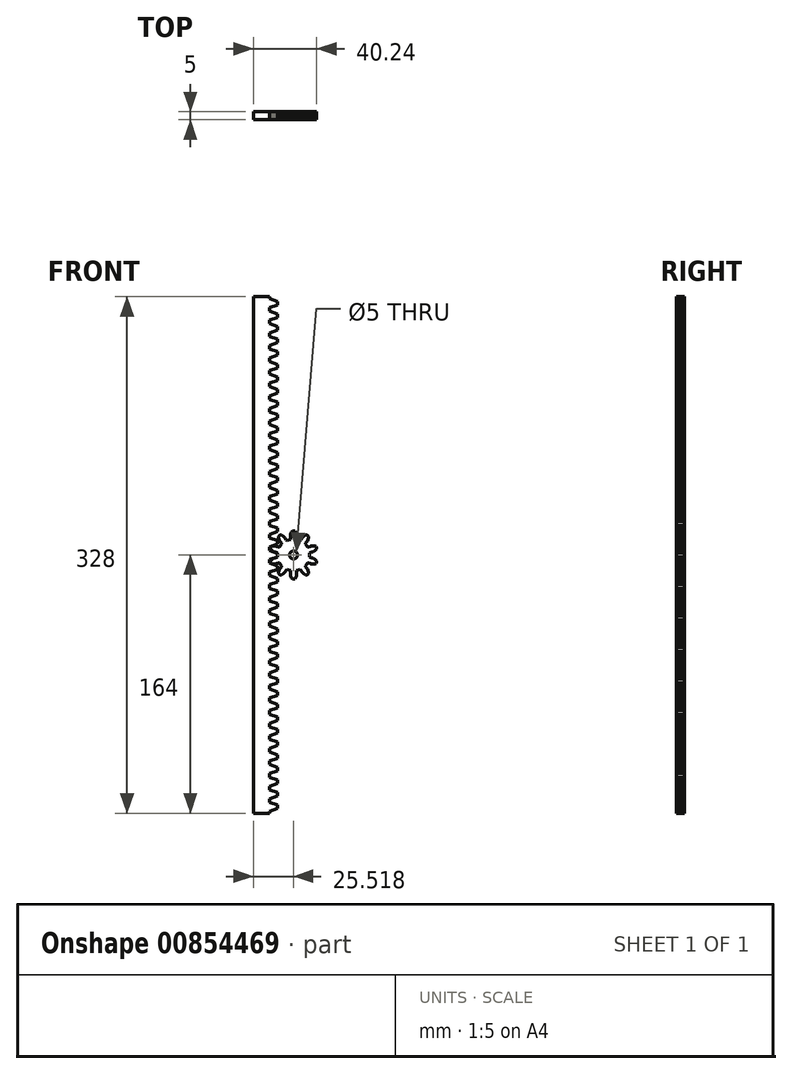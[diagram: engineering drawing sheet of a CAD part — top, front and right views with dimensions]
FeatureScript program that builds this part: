
annotation { "Feature Type Name" : "Feature", "Feature Type Description" : "" }
export const myFeature = defineFeature(function(context is Context, id is Id, definition is map)
    precondition{}
    {
        {
            var Q0;
            Q0=qCreatedBy(makeId("Front.planeOp"),FACE);
            var sketch = newSketch(context, id + "F0", { "sketchPlane" : qUnion([Q0])});
            skLineSegment(sketch, "E0", {"start": v(-9.93, -162.87) * mm, "end": v(-4.79, -161.12) * mm});
            skLineSegment(sketch, "E1", {"start": v(-4.79, -161.12) * mm, "end": v(-4.79, -158.88) * mm});
            skLineSegment(sketch, "E2", {"start": v(-4.79, -158.88) * mm, "end": v(-9.93, -157.13) * mm});
            skLineSegment(sketch, "E3", {"start": v(-9.93, -157.13) * mm, "end": v(-9.93, -154.87) * mm});
            skLineSegment(sketch, "E4", {"start": v(-9.93, -154.87) * mm, "end": v(-4.79, -153.12) * mm});
            skLineSegment(sketch, "E5", {"start": v(-4.79, -153.12) * mm, "end": v(-4.79, -150.88) * mm});
            skLineSegment(sketch, "E6", {"start": v(-4.79, -150.88) * mm, "end": v(-9.93, -149.13) * mm});
            skLineSegment(sketch, "E7", {"start": v(-9.93, -149.13) * mm, "end": v(-9.93, -146.87) * mm});
            skLineSegment(sketch, "E8", {"start": v(-9.93, -146.87) * mm, "end": v(-4.79, -145.12) * mm});
            skLineSegment(sketch, "E9", {"start": v(-4.79, -145.12) * mm, "end": v(-4.79, -142.88) * mm});
            skLineSegment(sketch, "E10", {"start": v(-4.79, -142.88) * mm, "end": v(-9.93, -141.13) * mm});
            skLineSegment(sketch, "E11", {"start": v(-9.93, -141.13) * mm, "end": v(-9.93, -138.87) * mm});
            skLineSegment(sketch, "E12", {"start": v(-9.93, -138.87) * mm, "end": v(-4.79, -137.12) * mm});
            skLineSegment(sketch, "E13", {"start": v(-4.79, -137.12) * mm, "end": v(-4.79, -134.88) * mm});
            skLineSegment(sketch, "E14", {"start": v(-4.79, -134.88) * mm, "end": v(-9.93, -133.13) * mm});
            skLineSegment(sketch, "E15", {"start": v(-9.93, -133.13) * mm, "end": v(-9.93, -130.87) * mm});
            skLineSegment(sketch, "E16", {"start": v(-9.93, -130.87) * mm, "end": v(-4.79, -129.12) * mm});
            skLineSegment(sketch, "E17", {"start": v(-4.79, -129.12) * mm, "end": v(-4.79, -126.88) * mm});
            skLineSegment(sketch, "E18", {"start": v(-4.79, -126.88) * mm, "end": v(-9.93, -125.13) * mm});
            skLineSegment(sketch, "E19", {"start": v(-9.93, -125.13) * mm, "end": v(-9.93, -122.87) * mm});
            skLineSegment(sketch, "E20", {"start": v(-9.93, -122.87) * mm, "end": v(-4.79, -121.12) * mm});
            skLineSegment(sketch, "E21", {"start": v(-4.79, -121.12) * mm, "end": v(-4.79, -118.88) * mm});
            skLineSegment(sketch, "E22", {"start": v(-4.79, -118.88) * mm, "end": v(-9.93, -117.13) * mm});
            skLineSegment(sketch, "E23", {"start": v(-9.93, -117.13) * mm, "end": v(-9.93, -114.87) * mm});
            skLineSegment(sketch, "E24", {"start": v(-9.93, -114.87) * mm, "end": v(-4.79, -113.12) * mm});
            skLineSegment(sketch, "E25", {"start": v(-4.79, -113.12) * mm, "end": v(-4.79, -110.88) * mm});
            skLineSegment(sketch, "E26", {"start": v(-4.79, -110.88) * mm, "end": v(-9.93, -109.13) * mm});
            skLineSegment(sketch, "E27", {"start": v(-9.93, -109.13) * mm, "end": v(-9.93, -106.87) * mm});
            skLineSegment(sketch, "E28", {"start": v(-9.93, -106.87) * mm, "end": v(-4.79, -105.12) * mm});
            skLineSegment(sketch, "E29", {"start": v(-4.79, -105.12) * mm, "end": v(-4.79, -102.88) * mm});
            skLineSegment(sketch, "E30", {"start": v(-4.79, -102.88) * mm, "end": v(-9.93, -101.13) * mm});
            skLineSegment(sketch, "E31", {"start": v(-9.93, -101.13) * mm, "end": v(-9.93, -98.87) * mm});
            skLineSegment(sketch, "E32", {"start": v(-9.93, -98.87) * mm, "end": v(-4.79, -97.12) * mm});
            skLineSegment(sketch, "E33", {"start": v(-4.79, -97.12) * mm, "end": v(-4.79, -94.88) * mm});
            skLineSegment(sketch, "E34", {"start": v(-4.79, -94.88) * mm, "end": v(-9.93, -93.13) * mm});
            skLineSegment(sketch, "E35", {"start": v(-9.93, -93.13) * mm, "end": v(-9.93, -90.87) * mm});
            skLineSegment(sketch, "E36", {"start": v(-9.93, -90.87) * mm, "end": v(-4.79, -89.12) * mm});
            skLineSegment(sketch, "E37", {"start": v(-4.79, -89.12) * mm, "end": v(-4.79, -86.88) * mm});
            skLineSegment(sketch, "E38", {"start": v(-4.79, -86.88) * mm, "end": v(-9.93, -85.13) * mm});
            skLineSegment(sketch, "E39", {"start": v(-9.93, -85.13) * mm, "end": v(-9.93, -82.87) * mm});
            skLineSegment(sketch, "E40", {"start": v(-9.93, -82.87) * mm, "end": v(-4.79, -81.12) * mm});
            skLineSegment(sketch, "E41", {"start": v(-4.79, -81.12) * mm, "end": v(-4.79, -78.88) * mm});
            skLineSegment(sketch, "E42", {"start": v(-4.79, -78.88) * mm, "end": v(-9.93, -77.13) * mm});
            skLineSegment(sketch, "E43", {"start": v(-9.93, -77.13) * mm, "end": v(-9.93, -74.87) * mm});
            skLineSegment(sketch, "E44", {"start": v(-9.93, -74.87) * mm, "end": v(-4.79, -73.12) * mm});
            skLineSegment(sketch, "E45", {"start": v(-4.79, -73.12) * mm, "end": v(-4.79, -70.88) * mm});
            skLineSegment(sketch, "E46", {"start": v(-4.79, -70.88) * mm, "end": v(-9.93, -69.13) * mm});
            skLineSegment(sketch, "E47", {"start": v(-9.93, -69.13) * mm, "end": v(-9.93, -66.87) * mm});
            skLineSegment(sketch, "E48", {"start": v(-9.93, -66.87) * mm, "end": v(-4.79, -65.12) * mm});
            skLineSegment(sketch, "E49", {"start": v(-4.79, -65.12) * mm, "end": v(-4.79, -62.88) * mm});
            skLineSegment(sketch, "E50", {"start": v(-4.79, -62.88) * mm, "end": v(-9.93, -61.13) * mm});
            skLineSegment(sketch, "E51", {"start": v(-9.93, -61.13) * mm, "end": v(-9.93, -58.87) * mm});
            skLineSegment(sketch, "E52", {"start": v(-9.93, -58.87) * mm, "end": v(-4.79, -57.12) * mm});
            skLineSegment(sketch, "E53", {"start": v(-4.79, -57.12) * mm, "end": v(-4.79, -54.88) * mm});
            skLineSegment(sketch, "E54", {"start": v(-4.79, -54.88) * mm, "end": v(-9.93, -53.13) * mm});
            skLineSegment(sketch, "E55", {"start": v(-9.93, -53.13) * mm, "end": v(-9.93, -50.87) * mm});
            skLineSegment(sketch, "E56", {"start": v(-9.93, -50.87) * mm, "end": v(-4.79, -49.12) * mm});
            skLineSegment(sketch, "E57", {"start": v(-4.79, -49.12) * mm, "end": v(-4.79, -46.88) * mm});
            skLineSegment(sketch, "E58", {"start": v(-4.79, -46.88) * mm, "end": v(-9.93, -45.13) * mm});
            skLineSegment(sketch, "E59", {"start": v(-9.93, -45.13) * mm, "end": v(-9.93, -42.87) * mm});
            skLineSegment(sketch, "E60", {"start": v(-9.93, -42.87) * mm, "end": v(-4.79, -41.12) * mm});
            skLineSegment(sketch, "E61", {"start": v(-4.79, -41.12) * mm, "end": v(-4.79, -38.88) * mm});
            skLineSegment(sketch, "E62", {"start": v(-4.79, -38.88) * mm, "end": v(-9.93, -37.13) * mm});
            skLineSegment(sketch, "E63", {"start": v(-9.93, -37.13) * mm, "end": v(-9.93, -34.87) * mm});
            skLineSegment(sketch, "E64", {"start": v(-9.93, -34.87) * mm, "end": v(-4.79, -33.12) * mm});
            skLineSegment(sketch, "E65", {"start": v(-4.79, -33.12) * mm, "end": v(-4.79, -30.88) * mm});
            skLineSegment(sketch, "E66", {"start": v(-4.79, -30.88) * mm, "end": v(-9.93, -29.13) * mm});
            skLineSegment(sketch, "E67", {"start": v(-9.93, -29.13) * mm, "end": v(-9.93, -26.87) * mm});
            skLineSegment(sketch, "E68", {"start": v(-9.93, -26.87) * mm, "end": v(-4.79, -25.12) * mm});
            skLineSegment(sketch, "E69", {"start": v(-4.79, -25.12) * mm, "end": v(-4.79, -22.88) * mm});
            skLineSegment(sketch, "E70", {"start": v(-4.79, -22.88) * mm, "end": v(-9.93, -21.13) * mm});
            skLineSegment(sketch, "E71", {"start": v(-9.93, -21.13) * mm, "end": v(-9.93, -18.87) * mm});
            skLineSegment(sketch, "E72", {"start": v(-9.93, -18.87) * mm, "end": v(-4.79, -17.12) * mm});
            skLineSegment(sketch, "E73", {"start": v(-4.79, -17.12) * mm, "end": v(-4.79, -14.88) * mm});
            skLineSegment(sketch, "E74", {"start": v(-4.79, -14.88) * mm, "end": v(-9.93, -13.13) * mm});
            skLineSegment(sketch, "E75", {"start": v(-9.93, -13.13) * mm, "end": v(-9.93, -10.87) * mm});
            skLineSegment(sketch, "E76", {"start": v(-9.93, -10.87) * mm, "end": v(-4.79, -9.12) * mm});
            skLineSegment(sketch, "E77", {"start": v(-4.79, -9.12) * mm, "end": v(-4.79, -6.88) * mm});
            skLineSegment(sketch, "E78", {"start": v(-4.79, -6.88) * mm, "end": v(-9.93, -5.13) * mm});
            skLineSegment(sketch, "E79", {"start": v(-9.93, -5.13) * mm, "end": v(-9.93, -2.87) * mm});
            skLineSegment(sketch, "E80", {"start": v(-9.93, -2.87) * mm, "end": v(-4.79, -1.12) * mm});
            skLineSegment(sketch, "E81", {"start": v(-4.79, -1.12) * mm, "end": v(-4.79, 1.12) * mm});
            skLineSegment(sketch, "E82", {"start": v(-4.79, 1.12) * mm, "end": v(-9.93, 2.87) * mm});
            skLineSegment(sketch, "E83", {"start": v(-9.93, 2.87) * mm, "end": v(-9.93, 5.13) * mm});
            skLineSegment(sketch, "E84", {"start": v(-9.93, 5.13) * mm, "end": v(-4.79, 6.88) * mm});
            skLineSegment(sketch, "E85", {"start": v(-4.79, 6.88) * mm, "end": v(-4.79, 9.12) * mm});
            skLineSegment(sketch, "E86", {"start": v(-4.79, 9.12) * mm, "end": v(-9.93, 10.87) * mm});
            skLineSegment(sketch, "E87", {"start": v(-9.93, 10.87) * mm, "end": v(-9.93, 13.13) * mm});
            skLineSegment(sketch, "E88", {"start": v(-9.93, 13.13) * mm, "end": v(-4.79, 14.88) * mm});
            skLineSegment(sketch, "E89", {"start": v(-4.79, 14.88) * mm, "end": v(-4.79, 17.12) * mm});
            skLineSegment(sketch, "E90", {"start": v(-4.79, 17.12) * mm, "end": v(-9.93, 18.87) * mm});
            skLineSegment(sketch, "E91", {"start": v(-9.93, 18.87) * mm, "end": v(-9.93, 21.13) * mm});
            skLineSegment(sketch, "E92", {"start": v(-9.93, 21.13) * mm, "end": v(-4.79, 22.88) * mm});
            skLineSegment(sketch, "E93", {"start": v(-4.79, 22.88) * mm, "end": v(-4.79, 25.12) * mm});
            skLineSegment(sketch, "E94", {"start": v(-4.79, 25.12) * mm, "end": v(-9.93, 26.87) * mm});
            skLineSegment(sketch, "E95", {"start": v(-9.93, 26.87) * mm, "end": v(-9.93, 29.13) * mm});
            skLineSegment(sketch, "E96", {"start": v(-9.93, 29.13) * mm, "end": v(-4.79, 30.88) * mm});
            skLineSegment(sketch, "E97", {"start": v(-4.79, 30.88) * mm, "end": v(-4.79, 33.12) * mm});
            skLineSegment(sketch, "E98", {"start": v(-4.79, 33.12) * mm, "end": v(-9.93, 34.87) * mm});
            skLineSegment(sketch, "E99", {"start": v(-9.93, 34.87) * mm, "end": v(-9.93, 37.13) * mm});
            skLineSegment(sketch, "E100", {"start": v(-9.93, 37.13) * mm, "end": v(-4.79, 38.88) * mm});
            skLineSegment(sketch, "E101", {"start": v(-4.79, 38.88) * mm, "end": v(-4.79, 41.12) * mm});
            skLineSegment(sketch, "E102", {"start": v(-4.79, 41.12) * mm, "end": v(-9.93, 42.87) * mm});
            skLineSegment(sketch, "E103", {"start": v(-9.93, 42.87) * mm, "end": v(-9.93, 45.13) * mm});
            skLineSegment(sketch, "E104", {"start": v(-9.93, 45.13) * mm, "end": v(-4.79, 46.88) * mm});
            skLineSegment(sketch, "E105", {"start": v(-4.79, 46.88) * mm, "end": v(-4.79, 49.12) * mm});
            skLineSegment(sketch, "E106", {"start": v(-4.79, 49.12) * mm, "end": v(-9.93, 50.87) * mm});
            skLineSegment(sketch, "E107", {"start": v(-9.93, 50.87) * mm, "end": v(-9.93, 53.13) * mm});
            skLineSegment(sketch, "E108", {"start": v(-9.93, 53.13) * mm, "end": v(-4.79, 54.88) * mm});
            skLineSegment(sketch, "E109", {"start": v(-4.79, 54.88) * mm, "end": v(-4.79, 57.12) * mm});
            skLineSegment(sketch, "E110", {"start": v(-4.79, 57.12) * mm, "end": v(-9.93, 58.87) * mm});
            skLineSegment(sketch, "E111", {"start": v(-9.93, 58.87) * mm, "end": v(-9.93, 61.13) * mm});
            skLineSegment(sketch, "E112", {"start": v(-9.93, 61.13) * mm, "end": v(-4.79, 62.88) * mm});
            skLineSegment(sketch, "E113", {"start": v(-4.79, 62.88) * mm, "end": v(-4.79, 65.12) * mm});
            skLineSegment(sketch, "E114", {"start": v(-4.79, 65.12) * mm, "end": v(-9.93, 66.87) * mm});
            skLineSegment(sketch, "E115", {"start": v(-9.93, 66.87) * mm, "end": v(-9.93, 69.13) * mm});
            skLineSegment(sketch, "E116", {"start": v(-9.93, 69.13) * mm, "end": v(-4.79, 70.88) * mm});
            skLineSegment(sketch, "E117", {"start": v(-4.79, 70.88) * mm, "end": v(-4.79, 73.12) * mm});
            skLineSegment(sketch, "E118", {"start": v(-4.79, 73.12) * mm, "end": v(-9.93, 74.87) * mm});
            skLineSegment(sketch, "E119", {"start": v(-9.93, 74.87) * mm, "end": v(-9.93, 77.13) * mm});
            skLineSegment(sketch, "E120", {"start": v(-9.93, 77.13) * mm, "end": v(-4.79, 78.88) * mm});
            skLineSegment(sketch, "E121", {"start": v(-4.79, 78.88) * mm, "end": v(-4.79, 81.12) * mm});
            skLineSegment(sketch, "E122", {"start": v(-4.79, 81.12) * mm, "end": v(-9.93, 82.87) * mm});
            skLineSegment(sketch, "E123", {"start": v(-9.93, 82.87) * mm, "end": v(-9.93, 85.13) * mm});
            skLineSegment(sketch, "E124", {"start": v(-9.93, 85.13) * mm, "end": v(-4.79, 86.88) * mm});
            skLineSegment(sketch, "E125", {"start": v(-4.79, 86.88) * mm, "end": v(-4.79, 89.12) * mm});
            skLineSegment(sketch, "E126", {"start": v(-4.79, 89.12) * mm, "end": v(-9.93, 90.87) * mm});
            skLineSegment(sketch, "E127", {"start": v(-9.93, 90.87) * mm, "end": v(-9.93, 93.13) * mm});
            skLineSegment(sketch, "E128", {"start": v(-9.93, 93.13) * mm, "end": v(-4.79, 94.88) * mm});
            skLineSegment(sketch, "E129", {"start": v(-4.79, 94.88) * mm, "end": v(-4.79, 97.12) * mm});
            skLineSegment(sketch, "E130", {"start": v(-4.79, 97.12) * mm, "end": v(-9.93, 98.87) * mm});
            skLineSegment(sketch, "E131", {"start": v(-9.93, 98.87) * mm, "end": v(-9.93, 101.13) * mm});
            skLineSegment(sketch, "E132", {"start": v(-9.93, 101.13) * mm, "end": v(-4.79, 102.88) * mm});
            skLineSegment(sketch, "E133", {"start": v(-4.79, 102.88) * mm, "end": v(-4.79, 105.12) * mm});
            skLineSegment(sketch, "E134", {"start": v(-4.79, 105.12) * mm, "end": v(-9.93, 106.87) * mm});
            skLineSegment(sketch, "E135", {"start": v(-9.93, 106.87) * mm, "end": v(-9.93, 109.13) * mm});
            skLineSegment(sketch, "E136", {"start": v(-9.93, 109.13) * mm, "end": v(-4.79, 110.88) * mm});
            skLineSegment(sketch, "E137", {"start": v(-4.79, 110.88) * mm, "end": v(-4.79, 113.12) * mm});
            skLineSegment(sketch, "E138", {"start": v(-4.79, 113.12) * mm, "end": v(-9.93, 114.87) * mm});
            skLineSegment(sketch, "E139", {"start": v(-9.93, 114.87) * mm, "end": v(-9.93, 117.13) * mm});
            skLineSegment(sketch, "E140", {"start": v(-9.93, 117.13) * mm, "end": v(-4.79, 118.88) * mm});
            skLineSegment(sketch, "E141", {"start": v(-4.79, 118.88) * mm, "end": v(-4.79, 121.12) * mm});
            skLineSegment(sketch, "E142", {"start": v(-4.79, 121.12) * mm, "end": v(-9.93, 122.87) * mm});
            skLineSegment(sketch, "E143", {"start": v(-9.93, 122.87) * mm, "end": v(-9.93, 125.13) * mm});
            skLineSegment(sketch, "E144", {"start": v(-9.93, 125.13) * mm, "end": v(-4.79, 126.88) * mm});
            skLineSegment(sketch, "E145", {"start": v(-4.79, 126.88) * mm, "end": v(-4.79, 129.12) * mm});
            skLineSegment(sketch, "E146", {"start": v(-4.79, 129.12) * mm, "end": v(-9.93, 130.87) * mm});
            skLineSegment(sketch, "E147", {"start": v(-9.93, 130.87) * mm, "end": v(-9.93, 133.13) * mm});
            skLineSegment(sketch, "E148", {"start": v(-9.93, 133.13) * mm, "end": v(-4.79, 134.88) * mm});
            skLineSegment(sketch, "E149", {"start": v(-4.79, 134.88) * mm, "end": v(-4.79, 137.12) * mm});
            skLineSegment(sketch, "E150", {"start": v(-4.79, 137.12) * mm, "end": v(-9.93, 138.87) * mm});
            skLineSegment(sketch, "E151", {"start": v(-9.93, 138.87) * mm, "end": v(-9.93, 141.13) * mm});
            skLineSegment(sketch, "E152", {"start": v(-9.93, 141.13) * mm, "end": v(-4.79, 142.88) * mm});
            skLineSegment(sketch, "E153", {"start": v(-4.79, 142.88) * mm, "end": v(-4.79, 145.12) * mm});
            skLineSegment(sketch, "E154", {"start": v(-4.79, 145.12) * mm, "end": v(-9.93, 146.87) * mm});
            skLineSegment(sketch, "E155", {"start": v(-9.93, 146.87) * mm, "end": v(-9.93, 149.13) * mm});
            skLineSegment(sketch, "E156", {"start": v(-9.93, 149.13) * mm, "end": v(-4.79, 150.88) * mm});
            skLineSegment(sketch, "E157", {"start": v(-4.79, 150.88) * mm, "end": v(-4.79, 153.12) * mm});
            skLineSegment(sketch, "E158", {"start": v(-4.79, 153.12) * mm, "end": v(-9.93, 154.87) * mm});
            skLineSegment(sketch, "E159", {"start": v(-9.93, 154.87) * mm, "end": v(-9.93, 157.13) * mm});
            skLineSegment(sketch, "E160", {"start": v(-9.93, 157.13) * mm, "end": v(-4.79, 158.88) * mm});
            skLineSegment(sketch, "E161", {"start": v(-4.79, 158.88) * mm, "end": v(-4.79, 161.12) * mm});
            skLineSegment(sketch, "E162", {"start": v(-4.79, 161.12) * mm, "end": v(-9.93, 162.87) * mm});
            skLineSegment(sketch, "E163", {"start": v(-9.93, 162.87) * mm, "end": v(-9.93, 164) * mm});
            skLineSegment(sketch, "E164", {"start": v(-9.93, 164) * mm, "end": v(-20.12, 164) * mm});
            skLineSegment(sketch, "E165", {"start": v(-20.12, 164) * mm, "end": v(-20.12, -164) * mm});
            skLineSegment(sketch, "E166", {"start": v(-20.12, -164) * mm, "end": v(-9.93, -164) * mm});
            skLineSegment(sketch, "E167", {"start": v(-9.93, -164) * mm, "end": v(-9.93, -162.87) * mm});
            skLineSegment(sketch, "E168", {"start": v(-8.83, 5.46) * mm, "end": v(-9.13, 4.72) * mm});
            skLineSegment(sketch, "E169", {"start": v(-9.13, 4.72) * mm, "end": v(-9.32, 3.94) * mm});
            skLineSegment(sketch, "E170", {"start": v(-9.32, 3.94) * mm, "end": v(-8.99, 3.46) * mm});
            skLineSegment(sketch, "E171", {"start": v(-8.99, 3.46) * mm, "end": v(-7.87, 2.43) * mm});
            skLineSegment(sketch, "E172", {"start": v(-7.87, 2.43) * mm, "end": v(-7.02, 1.92) * mm});
            skLineSegment(sketch, "E173", {"start": v(-7.02, 1.92) * mm, "end": v(-6.61, 1.78) * mm});
            skLineSegment(sketch, "E174", {"start": v(-6.61, 1.78) * mm, "end": v(-6.5, 1.79) * mm});
            skLineSegment(sketch, "E175", {"start": v(-6.5, 1.79) * mm, "end": v(-5.3, 1.61) * mm});
            skLineSegment(sketch, "E176", {"start": v(-5.3, 1.61) * mm, "end": v(-4.74, 1.14) * mm});
            skLineSegment(sketch, "E177", {"start": v(-4.74, 1.14) * mm, "end": v(-4.74, -1.14) * mm});
            skLineSegment(sketch, "E178", {"start": v(-4.74, -1.14) * mm, "end": v(-5.3, -1.61) * mm});
            skLineSegment(sketch, "E179", {"start": v(-5.3, -1.61) * mm, "end": v(-6.5, -1.79) * mm});
            skLineSegment(sketch, "E180", {"start": v(-6.5, -1.79) * mm, "end": v(-6.61, -1.78) * mm});
            skLineSegment(sketch, "E181", {"start": v(-6.61, -1.78) * mm, "end": v(-7.02, -1.92) * mm});
            skLineSegment(sketch, "E182", {"start": v(-7.02, -1.92) * mm, "end": v(-7.87, -2.43) * mm});
            skLineSegment(sketch, "E183", {"start": v(-7.87, -2.43) * mm, "end": v(-8.99, -3.46) * mm});
            skLineSegment(sketch, "E184", {"start": v(-8.99, -3.46) * mm, "end": v(-9.32, -3.94) * mm});
            skLineSegment(sketch, "E185", {"start": v(-9.32, -3.94) * mm, "end": v(-9.13, -4.72) * mm});
            skLineSegment(sketch, "E186", {"start": v(-9.13, -4.72) * mm, "end": v(-8.83, -5.46) * mm});
            skLineSegment(sketch, "E187", {"start": v(-8.83, -5.46) * mm, "end": v(-8.28, -5.65) * mm});
            skLineSegment(sketch, "E188", {"start": v(-8.28, -5.65) * mm, "end": v(-6.76, -5.83) * mm});
            skLineSegment(sketch, "E189", {"start": v(-6.76, -5.83) * mm, "end": v(-5.77, -5.75) * mm});
            skLineSegment(sketch, "E190", {"start": v(-5.77, -5.75) * mm, "end": v(-5.36, -5.62) * mm});
            skLineSegment(sketch, "E191", {"start": v(-5.36, -5.62) * mm, "end": v(-5.27, -5.54) * mm});
            skLineSegment(sketch, "E192", {"start": v(-5.27, -5.54) * mm, "end": v(-4.21, -4.99) * mm});
            skLineSegment(sketch, "E193", {"start": v(-4.21, -4.99) * mm, "end": v(-3.47, -5.04) * mm});
            skLineSegment(sketch, "E194", {"start": v(-3.47, -5.04) * mm, "end": v(-2.13, -6.88) * mm});
            skLineSegment(sketch, "E195", {"start": v(-2.13, -6.88) * mm, "end": v(-2.31, -7.6) * mm});
            skLineSegment(sketch, "E196", {"start": v(-2.31, -7.6) * mm, "end": v(-3.17, -8.44) * mm});
            skLineSegment(sketch, "E197", {"start": v(-3.17, -8.44) * mm, "end": v(-3.27, -8.5) * mm});
            skLineSegment(sketch, "E198", {"start": v(-3.27, -8.5) * mm, "end": v(-3.52, -8.85) * mm});
            skLineSegment(sketch, "E199", {"start": v(-3.52, -8.85) * mm, "end": v(-3.9, -9.76) * mm});
            skLineSegment(sketch, "E200", {"start": v(-3.9, -9.76) * mm, "end": v(-4.2, -11.26) * mm});
            skLineSegment(sketch, "E201", {"start": v(-4.2, -11.26) * mm, "end": v(-4.2, -11.84) * mm});
            skLineSegment(sketch, "E202", {"start": v(-4.2, -11.84) * mm, "end": v(-3.58, -12.36) * mm});
            skLineSegment(sketch, "E203", {"start": v(-3.58, -12.36) * mm, "end": v(-2.9, -12.78) * mm});
            skLineSegment(sketch, "E204", {"start": v(-2.9, -12.78) * mm, "end": v(-2.34, -12.6) * mm});
            skLineSegment(sketch, "E205", {"start": v(-2.34, -12.6) * mm, "end": v(-1.01, -11.87) * mm});
            skLineSegment(sketch, "E206", {"start": v(-1.01, -11.87) * mm, "end": v(-0.26, -11.21) * mm});
            skLineSegment(sketch, "E207", {"start": v(-0.26, -11.21) * mm, "end": v(0, -10.87) * mm});
            skLineSegment(sketch, "E208", {"start": v(0, -10.87) * mm, "end": v(0.02, -10.76) * mm});
            skLineSegment(sketch, "E209", {"start": v(0.02, -10.76) * mm, "end": v(0.55, -9.68) * mm});
            skLineSegment(sketch, "E210", {"start": v(0.55, -9.68) * mm, "end": v(1.18, -9.29) * mm});
            skLineSegment(sketch, "E211", {"start": v(1.18, -9.29) * mm, "end": v(3.35, -10) * mm});
            skLineSegment(sketch, "E212", {"start": v(3.35, -10) * mm, "end": v(3.63, -10.68) * mm});
            skLineSegment(sketch, "E213", {"start": v(3.63, -10.68) * mm, "end": v(3.43, -11.86) * mm});
            skLineSegment(sketch, "E214", {"start": v(3.43, -11.86) * mm, "end": v(3.38, -11.97) * mm});
            skLineSegment(sketch, "E215", {"start": v(3.38, -11.97) * mm, "end": v(3.39, -12.4) * mm});
            skLineSegment(sketch, "E216", {"start": v(3.39, -12.4) * mm, "end": v(3.6, -13.37) * mm});
            skLineSegment(sketch, "E217", {"start": v(3.6, -13.37) * mm, "end": v(4.25, -14.75) * mm});
            skLineSegment(sketch, "E218", {"start": v(4.25, -14.75) * mm, "end": v(4.6, -15.22) * mm});
            skLineSegment(sketch, "E219", {"start": v(4.6, -15.22) * mm, "end": v(5.4, -15.28) * mm});
            skLineSegment(sketch, "E220", {"start": v(5.4, -15.28) * mm, "end": v(6.2, -15.22) * mm});
            skLineSegment(sketch, "E221", {"start": v(6.2, -15.22) * mm, "end": v(6.55, -14.75) * mm});
            skLineSegment(sketch, "E222", {"start": v(6.55, -14.75) * mm, "end": v(7.19, -13.37) * mm});
            skLineSegment(sketch, "E223", {"start": v(7.19, -13.37) * mm, "end": v(7.41, -12.4) * mm});
            skLineSegment(sketch, "E224", {"start": v(7.41, -12.4) * mm, "end": v(7.42, -11.97) * mm});
            skLineSegment(sketch, "E225", {"start": v(7.42, -11.97) * mm, "end": v(7.37, -11.86) * mm});
            skLineSegment(sketch, "E226", {"start": v(7.37, -11.86) * mm, "end": v(7.17, -10.68) * mm});
            skLineSegment(sketch, "E227", {"start": v(7.17, -10.68) * mm, "end": v(7.45, -10) * mm});
            skLineSegment(sketch, "E228", {"start": v(7.45, -10) * mm, "end": v(9.61, -9.29) * mm});
            skLineSegment(sketch, "E229", {"start": v(9.61, -9.29) * mm, "end": v(10.24, -9.68) * mm});
            skLineSegment(sketch, "E230", {"start": v(10.24, -9.68) * mm, "end": v(10.78, -10.76) * mm});
            skLineSegment(sketch, "E231", {"start": v(10.78, -10.76) * mm, "end": v(10.8, -10.87) * mm});
            skLineSegment(sketch, "E232", {"start": v(10.8, -10.87) * mm, "end": v(11.06, -11.21) * mm});
            skLineSegment(sketch, "E233", {"start": v(11.06, -11.21) * mm, "end": v(11.8, -11.87) * mm});
            skLineSegment(sketch, "E234", {"start": v(11.8, -11.87) * mm, "end": v(13.14, -12.6) * mm});
            skLineSegment(sketch, "E235", {"start": v(13.14, -12.6) * mm, "end": v(13.7, -12.78) * mm});
            skLineSegment(sketch, "E236", {"start": v(13.7, -12.78) * mm, "end": v(14.38, -12.36) * mm});
            skLineSegment(sketch, "E237", {"start": v(14.38, -12.36) * mm, "end": v(14.99, -11.84) * mm});
            skLineSegment(sketch, "E238", {"start": v(14.99, -11.84) * mm, "end": v(15, -11.26) * mm});
            skLineSegment(sketch, "E239", {"start": v(15, -11.26) * mm, "end": v(14.7, -9.76) * mm});
            skLineSegment(sketch, "E240", {"start": v(14.7, -9.76) * mm, "end": v(14.31, -8.85) * mm});
            skLineSegment(sketch, "E241", {"start": v(14.31, -8.85) * mm, "end": v(14.07, -8.5) * mm});
            skLineSegment(sketch, "E242", {"start": v(14.07, -8.5) * mm, "end": v(13.97, -8.44) * mm});
            skLineSegment(sketch, "E243", {"start": v(13.97, -8.44) * mm, "end": v(13.11, -7.6) * mm});
            skLineSegment(sketch, "E244", {"start": v(13.11, -7.6) * mm, "end": v(12.93, -6.88) * mm});
            skLineSegment(sketch, "E245", {"start": v(12.93, -6.88) * mm, "end": v(14.27, -5.04) * mm});
            skLineSegment(sketch, "E246", {"start": v(14.27, -5.04) * mm, "end": v(15, -4.99) * mm});
            skLineSegment(sketch, "E247", {"start": v(15, -4.99) * mm, "end": v(16.07, -5.54) * mm});
            skLineSegment(sketch, "E248", {"start": v(16.07, -5.54) * mm, "end": v(16.16, -5.62) * mm});
            skLineSegment(sketch, "E249", {"start": v(16.16, -5.62) * mm, "end": v(16.57, -5.75) * mm});
            skLineSegment(sketch, "E250", {"start": v(16.57, -5.75) * mm, "end": v(17.56, -5.83) * mm});
            skLineSegment(sketch, "E251", {"start": v(17.56, -5.83) * mm, "end": v(19.07, -5.65) * mm});
            skLineSegment(sketch, "E252", {"start": v(19.07, -5.65) * mm, "end": v(19.62, -5.46) * mm});
            skLineSegment(sketch, "E253", {"start": v(19.62, -5.46) * mm, "end": v(19.93, -4.72) * mm});
            skLineSegment(sketch, "E254", {"start": v(19.93, -4.72) * mm, "end": v(20.12, -3.94) * mm});
            skLineSegment(sketch, "E255", {"start": v(20.12, -3.94) * mm, "end": v(19.78, -3.46) * mm});
            skLineSegment(sketch, "E256", {"start": v(19.78, -3.46) * mm, "end": v(18.67, -2.43) * mm});
            skLineSegment(sketch, "E257", {"start": v(18.67, -2.43) * mm, "end": v(17.81, -1.92) * mm});
            skLineSegment(sketch, "E258", {"start": v(17.81, -1.92) * mm, "end": v(17.4, -1.78) * mm});
            skLineSegment(sketch, "E259", {"start": v(17.4, -1.78) * mm, "end": v(17.3, -1.79) * mm});
            skLineSegment(sketch, "E260", {"start": v(17.3, -1.79) * mm, "end": v(16.1, -1.61) * mm});
            skLineSegment(sketch, "E261", {"start": v(16.1, -1.61) * mm, "end": v(15.53, -1.14) * mm});
            skLineSegment(sketch, "E262", {"start": v(15.53, -1.14) * mm, "end": v(15.53, 1.14) * mm});
            skLineSegment(sketch, "E263", {"start": v(15.53, 1.14) * mm, "end": v(16.1, 1.61) * mm});
            skLineSegment(sketch, "E264", {"start": v(16.1, 1.61) * mm, "end": v(17.3, 1.79) * mm});
            skLineSegment(sketch, "E265", {"start": v(17.3, 1.79) * mm, "end": v(17.4, 1.78) * mm});
            skLineSegment(sketch, "E266", {"start": v(17.4, 1.78) * mm, "end": v(17.81, 1.92) * mm});
            skLineSegment(sketch, "E267", {"start": v(17.81, 1.92) * mm, "end": v(18.67, 2.43) * mm});
            skLineSegment(sketch, "E268", {"start": v(18.67, 2.43) * mm, "end": v(19.78, 3.46) * mm});
            skLineSegment(sketch, "E269", {"start": v(19.78, 3.46) * mm, "end": v(20.12, 3.94) * mm});
            skLineSegment(sketch, "E270", {"start": v(20.12, 3.94) * mm, "end": v(19.93, 4.72) * mm});
            skLineSegment(sketch, "E271", {"start": v(19.93, 4.72) * mm, "end": v(19.62, 5.46) * mm});
            skLineSegment(sketch, "E272", {"start": v(19.62, 5.46) * mm, "end": v(19.07, 5.65) * mm});
            skLineSegment(sketch, "E273", {"start": v(19.07, 5.65) * mm, "end": v(17.56, 5.83) * mm});
            skLineSegment(sketch, "E274", {"start": v(17.56, 5.83) * mm, "end": v(16.57, 5.75) * mm});
            skLineSegment(sketch, "E275", {"start": v(16.57, 5.75) * mm, "end": v(16.16, 5.62) * mm});
            skLineSegment(sketch, "E276", {"start": v(16.16, 5.62) * mm, "end": v(16.07, 5.54) * mm});
            skLineSegment(sketch, "E277", {"start": v(16.07, 5.54) * mm, "end": v(15, 4.99) * mm});
            skLineSegment(sketch, "E278", {"start": v(15, 4.99) * mm, "end": v(14.27, 5.04) * mm});
            skLineSegment(sketch, "E279", {"start": v(14.27, 5.04) * mm, "end": v(12.93, 6.88) * mm});
            skLineSegment(sketch, "E280", {"start": v(12.93, 6.88) * mm, "end": v(13.11, 7.6) * mm});
            skLineSegment(sketch, "E281", {"start": v(13.11, 7.6) * mm, "end": v(13.97, 8.44) * mm});
            skLineSegment(sketch, "E282", {"start": v(13.97, 8.44) * mm, "end": v(14.07, 8.5) * mm});
            skLineSegment(sketch, "E283", {"start": v(14.07, 8.5) * mm, "end": v(14.31, 8.85) * mm});
            skLineSegment(sketch, "E284", {"start": v(14.31, 8.85) * mm, "end": v(14.7, 9.76) * mm});
            skLineSegment(sketch, "E285", {"start": v(14.7, 9.76) * mm, "end": v(15, 11.26) * mm});
            skLineSegment(sketch, "E286", {"start": v(15, 11.26) * mm, "end": v(14.99, 11.84) * mm});
            skLineSegment(sketch, "E287", {"start": v(14.99, 11.84) * mm, "end": v(14.38, 12.36) * mm});
            skLineSegment(sketch, "E288", {"start": v(14.38, 12.36) * mm, "end": v(13.7, 12.78) * mm});
            skLineSegment(sketch, "E289", {"start": v(13.7, 12.78) * mm, "end": v(13.14, 12.6) * mm});
            skLineSegment(sketch, "E290", {"start": v(13.14, 12.6) * mm, "end": v(11.8, 11.87) * mm});
            skLineSegment(sketch, "E291", {"start": v(11.8, 11.87) * mm, "end": v(11.06, 11.21) * mm});
            skLineSegment(sketch, "E292", {"start": v(11.06, 11.21) * mm, "end": v(10.8, 10.87) * mm});
            skLineSegment(sketch, "E293", {"start": v(10.8, 10.87) * mm, "end": v(10.78, 10.76) * mm});
            skLineSegment(sketch, "E294", {"start": v(10.78, 10.76) * mm, "end": v(10.24, 9.68) * mm});
            skLineSegment(sketch, "E295", {"start": v(10.24, 9.68) * mm, "end": v(9.61, 9.29) * mm});
            skLineSegment(sketch, "E296", {"start": v(9.61, 9.29) * mm, "end": v(7.45, 10) * mm});
            skLineSegment(sketch, "E297", {"start": v(7.45, 10) * mm, "end": v(7.17, 10.68) * mm});
            skLineSegment(sketch, "E298", {"start": v(7.17, 10.68) * mm, "end": v(7.37, 11.86) * mm});
            skLineSegment(sketch, "E299", {"start": v(7.37, 11.86) * mm, "end": v(7.42, 11.97) * mm});
            skLineSegment(sketch, "E300", {"start": v(7.42, 11.97) * mm, "end": v(7.41, 12.4) * mm});
            skLineSegment(sketch, "E301", {"start": v(7.41, 12.4) * mm, "end": v(7.19, 13.37) * mm});
            skLineSegment(sketch, "E302", {"start": v(7.19, 13.37) * mm, "end": v(6.55, 14.75) * mm});
            skLineSegment(sketch, "E303", {"start": v(6.55, 14.75) * mm, "end": v(6.2, 15.22) * mm});
            skLineSegment(sketch, "E304", {"start": v(6.2, 15.22) * mm, "end": v(5.4, 15.28) * mm});
            skLineSegment(sketch, "E305", {"start": v(5.4, 15.28) * mm, "end": v(4.6, 15.22) * mm});
            skLineSegment(sketch, "E306", {"start": v(4.6, 15.22) * mm, "end": v(4.25, 14.75) * mm});
            skLineSegment(sketch, "E307", {"start": v(4.25, 14.75) * mm, "end": v(3.6, 13.37) * mm});
            skLineSegment(sketch, "E308", {"start": v(3.6, 13.37) * mm, "end": v(3.39, 12.4) * mm});
            skLineSegment(sketch, "E309", {"start": v(3.39, 12.4) * mm, "end": v(3.38, 11.97) * mm});
            skLineSegment(sketch, "E310", {"start": v(3.38, 11.97) * mm, "end": v(3.43, 11.86) * mm});
            skLineSegment(sketch, "E311", {"start": v(3.43, 11.86) * mm, "end": v(3.63, 10.68) * mm});
            skLineSegment(sketch, "E312", {"start": v(3.63, 10.68) * mm, "end": v(3.35, 10) * mm});
            skLineSegment(sketch, "E313", {"start": v(3.35, 10) * mm, "end": v(1.18, 9.29) * mm});
            skLineSegment(sketch, "E314", {"start": v(1.18, 9.29) * mm, "end": v(0.55, 9.68) * mm});
            skLineSegment(sketch, "E315", {"start": v(0.55, 9.68) * mm, "end": v(0.02, 10.76) * mm});
            skLineSegment(sketch, "E316", {"start": v(0.02, 10.76) * mm, "end": v(0, 10.87) * mm});
            skLineSegment(sketch, "E317", {"start": v(0, 10.87) * mm, "end": v(-0.26, 11.21) * mm});
            skLineSegment(sketch, "E318", {"start": v(-0.26, 11.21) * mm, "end": v(-1.01, 11.87) * mm});
            skLineSegment(sketch, "E319", {"start": v(-1.01, 11.87) * mm, "end": v(-2.34, 12.6) * mm});
            skLineSegment(sketch, "E320", {"start": v(-2.34, 12.6) * mm, "end": v(-2.9, 12.78) * mm});
            skLineSegment(sketch, "E321", {"start": v(-2.9, 12.78) * mm, "end": v(-3.58, 12.36) * mm});
            skLineSegment(sketch, "E322", {"start": v(-3.58, 12.36) * mm, "end": v(-4.2, 11.84) * mm});
            skLineSegment(sketch, "E323", {"start": v(-4.2, 11.84) * mm, "end": v(-4.2, 11.26) * mm});
            skLineSegment(sketch, "E324", {"start": v(-4.2, 11.26) * mm, "end": v(-3.9, 9.76) * mm});
            skLineSegment(sketch, "E325", {"start": v(-3.9, 9.76) * mm, "end": v(-3.52, 8.85) * mm});
            skLineSegment(sketch, "E326", {"start": v(-3.52, 8.85) * mm, "end": v(-3.27, 8.5) * mm});
            skLineSegment(sketch, "E327", {"start": v(-3.27, 8.5) * mm, "end": v(-3.17, 8.44) * mm});
            skLineSegment(sketch, "E328", {"start": v(-3.17, 8.44) * mm, "end": v(-2.31, 7.6) * mm});
            skLineSegment(sketch, "E329", {"start": v(-2.31, 7.6) * mm, "end": v(-2.13, 6.88) * mm});
            skLineSegment(sketch, "E330", {"start": v(-2.13, 6.88) * mm, "end": v(-3.47, 5.04) * mm});
            skLineSegment(sketch, "E331", {"start": v(-3.47, 5.04) * mm, "end": v(-4.21, 4.99) * mm});
            skLineSegment(sketch, "E332", {"start": v(-4.21, 4.99) * mm, "end": v(-5.27, 5.54) * mm});
            skLineSegment(sketch, "E333", {"start": v(-5.27, 5.54) * mm, "end": v(-5.36, 5.62) * mm});
            skLineSegment(sketch, "E334", {"start": v(-5.36, 5.62) * mm, "end": v(-5.77, 5.75) * mm});
            skLineSegment(sketch, "E335", {"start": v(-5.77, 5.75) * mm, "end": v(-6.76, 5.83) * mm});
            skLineSegment(sketch, "E336", {"start": v(-6.76, 5.83) * mm, "end": v(-8.28, 5.65) * mm});
            skLineSegment(sketch, "E337", {"start": v(-8.28, 5.65) * mm, "end": v(-8.83, 5.46) * mm});
            skCircle(sketch, "E338", {"center": v(5.4, 0) * mm, "radius": 2.5 * mm});
            skSolve(sketch);
        }
        {
            var Q0;
            Q0=makeQuery(id+"F0.imprint","IMPRINT",FACE,{"disambiguationData":[TD([[makeQuery(id+"F0.imprint","IMPRINT",EDGE,{"derivedFrom":sQuery(id+"F0.wireOp",EDGE,"E168")}),1.0]])]});
            var Q1;
            Q1=makeQuery(id+"F0.imprint","IMPRINT",FACE,{"disambiguationData":[TD([[makeQuery(id+"F0.imprint","IMPRINT",EDGE,{"derivedFrom":sQuery(id+"F0.wireOp",EDGE,"E0")}),1.0]])]});
            extrude(context, id + "F1", {"entities" : qUnion([Q0, Q1]), "depth" : 5 * mm, "offsetDistance" : 25 * mm});
        }
    });
